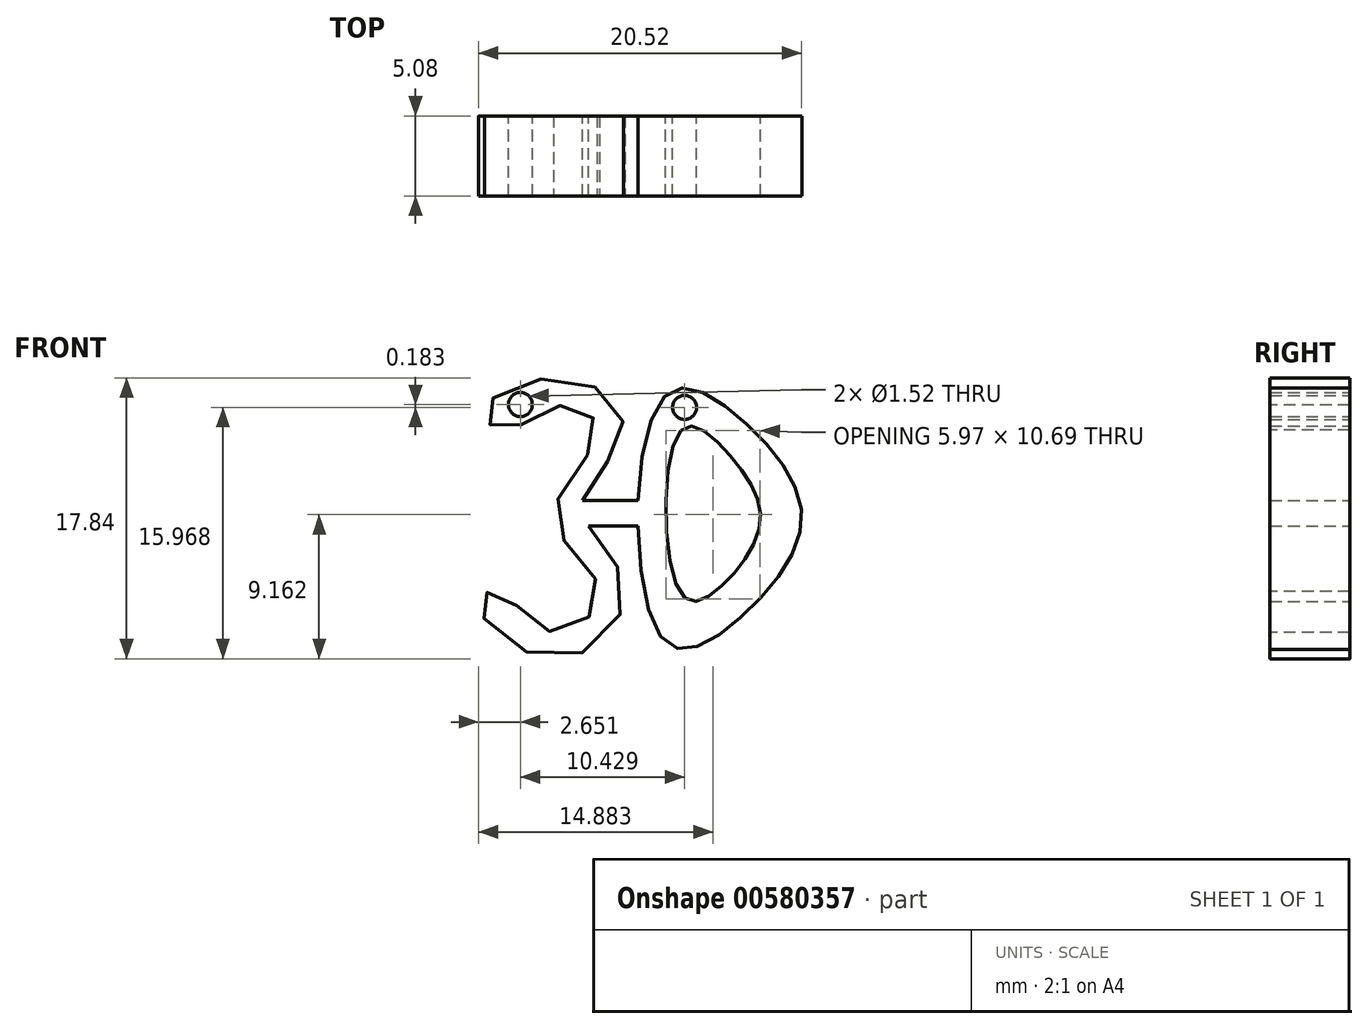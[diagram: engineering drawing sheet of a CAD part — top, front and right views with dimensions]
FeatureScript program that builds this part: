
annotation { "Feature Type Name" : "Feature", "Feature Type Description" : "" }
export const myFeature = defineFeature(function(context is Context, id is Id, definition is map)
    precondition{}
    {
        {
            var Q0;
            Q0=qCreatedBy(makeId("Front.planeOp"),FACE);
            var sketch = newSketch(context, id + "F0", { "sketchPlane" : qUnion([Q0])});
            skPoint(sketch, "E0.middle", {"position": v(1.86, -1.86) * mm});
            skFitSpline(sketch, "E1", {"points": [v(-9.45, 5.04) * mm, v(-3.92, 6.94) * mm, v(-0.71, 3.5) * mm, v(-3.33, -1.14) * mm, v(-0.58, -6.22) * mm, v(-4.82, -10.82) * mm, v(-9.87, -7.32) * mm, v(-8.57, -6.6) * mm, v(-5.2, -9.11) * mm, v(-2.18, -6.57) * mm, v(-5.12, -1.86) * mm, v(-2.34, 3.51) * mm, v(-4.41, 5.3) * mm, v(-8.33, 3.7) * mm, v(-9.45, 5.04) * mm]});
            skFitSpline(sketch, "E2", {"points": [v(1.86, 5.77) * mm, v(1.86, -9.62) * mm, v(6.8, -8.16) * mm, v(10.65, -1.86) * mm, v(6.9, 4.32) * mm, v(1.86, 5.77) * mm]});
            skFitSpline(sketch, "E3", {"points": [v(2.99, 3.69) * mm, v(3.07, -6.81) * mm, v(5.8, -5.96) * mm, v(8.02, -1.86) * mm, v(5.9, 2.32) * mm, v(2.99, 3.69) * mm]});
            skLineSegment(sketch, "E4", {"start": v(-3.28, -0.77) * mm, "end": v(0.26, -0.77) * mm});
            skLineSegment(sketch, "E5", {"start": v(0.24, -2.38) * mm, "end": v(-2.9, -2.38) * mm});
            skCircle(sketch, "E6", {"center": v(-7.22, 5.33) * mm, "radius": 0.76 * mm});
            skCircle(sketch, "E7", {"center": v(3.2, 5.15) * mm, "radius": 0.76 * mm});
            skSolve(sketch);
        }
        {
            var Q0;
            Q0 = qSketchRegion(id + "F0", true);
            extrude(context, id + "F1", {"entities" : qUnion([Q0]), "depth" : 5.08 * mm, "offsetDistance" : 25.4 * mm});
        }
    });
